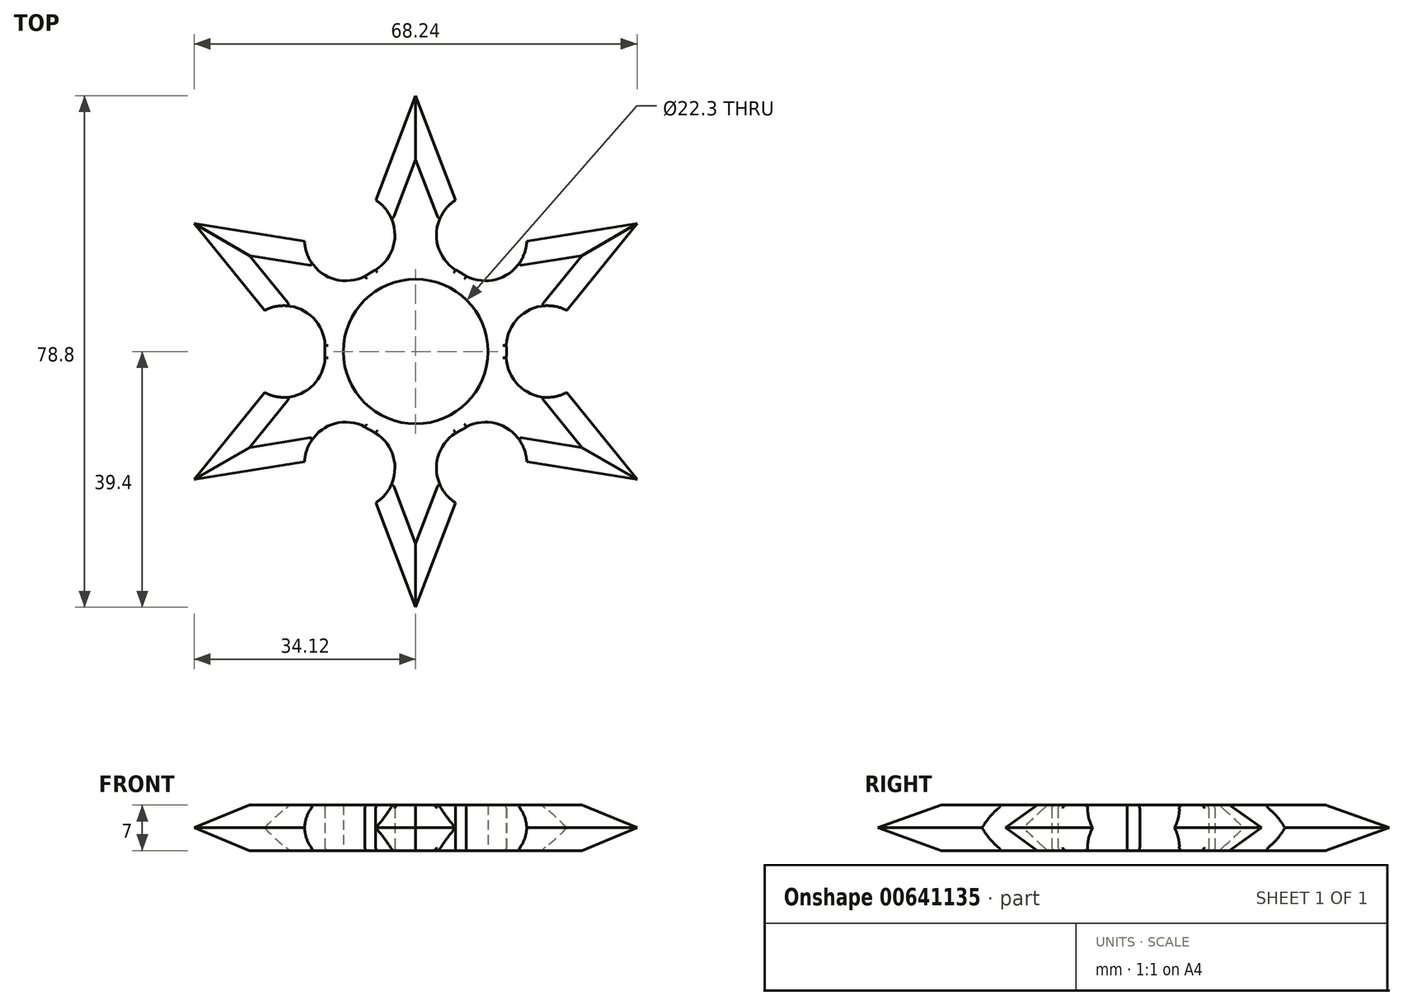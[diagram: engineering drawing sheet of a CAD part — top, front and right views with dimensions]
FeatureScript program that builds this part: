
annotation { "Feature Type Name" : "Feature", "Feature Type Description" : "" }
export const myFeature = defineFeature(function(context is Context, id is Id, definition is map)
    precondition{}
    {
        {
            var Q0;
            Q0=qCreatedBy(makeId("Top.planeOp"),FACE);
            var sketch = newSketch(context, id + "F0", { "sketchPlane" : qUnion([Q0])});
            skCircle(sketch, "E0", {"center": v(0, 0) * mm, "radius": 11.15 * mm});
            skCircle(sketch, "E1", {"center": v(0, 0) * mm, "radius": 14 * mm});
            skLineSegment(sketch, "E2", {"start": v(0, 0) * mm, "end": v(0, 43.6) * mm, "construction": true});
            skLineSegment(sketch, "E3.MirrorCS", {"start": v(0, 0) * mm, "end": v(37.76, -21.8) * mm, "construction": true});
            skLineSegment(sketch, "E4.MirrorCS", {"start": v(0, 0) * mm, "end": v(-37.76, -21.8) * mm, "construction": true});
            skLineSegment(sketch, "E5.MirrorCS", {"start": v(0, 0) * mm, "end": v(-37.76, 21.8) * mm, "construction": true});
            skLineSegment(sketch, "E6", {"start": v(0, 0) * mm, "end": v(0, -43.6) * mm, "construction": true});
            skLineSegment(sketch, "E7", {"start": v(20.76, 11.98) * mm, "end": v(24.5, 5.49) * mm});
            skLineSegment(sketch, "E8.MirrorCS", {"start": v(20.76, 11.98) * mm, "end": v(17, 18.48) * mm});
            skLineSegment(sketch, "E9", {"start": v(37.76, 21.8) * mm, "end": v(17, 18.48) * mm});
            skLineSegment(sketch, "E10", {"start": v(24.5, 5.49) * mm, "end": v(37.76, 21.8) * mm});
            skLineSegment(sketch, "E11", {"start": v(0, 0) * mm, "end": v(7, 12.12) * mm, "construction": true});
            skArc(sketch, "E12", {"start": v(7, 12.12) * mm, "mid": v(14.18, 11.88) * mm, "end": v(17, 18.48) * mm});
            skArc(sketch, "E13.MirrorCS", {"start": v(14, 0) * mm, "mid": v(17.38, 6.34) * mm, "end": v(24.5, 5.49) * mm});
            skLineSegment(sketch, "E14.MirrorCS", {"start": v(-37.76, 21.8) * mm, "end": v(-17, 18.48) * mm});
            skLineSegment(sketch, "E15.MirrorCS", {"start": v(-20.76, 11.98) * mm, "end": v(-17, 18.48) * mm});
            skArc(sketch, "E16.MirrorCS", {"start": v(-7, 12.12) * mm, "mid": v(-14.18, 11.88) * mm, "end": v(-17, 18.48) * mm});
            skArc(sketch, "E17.MirrorCS", {"start": v(-14, 0) * mm, "mid": v(-17.38, 6.34) * mm, "end": v(-24.5, 5.49) * mm});
            skLineSegment(sketch, "E18.MirrorCS", {"start": v(-20.76, 11.98) * mm, "end": v(-24.5, 5.49) * mm});
            skLineSegment(sketch, "E19.MirrorCS", {"start": v(-24.5, 5.49) * mm, "end": v(-37.76, 21.8) * mm});
            skArc(sketch, "E20.MirrorCS", {"start": v(7, -12.12) * mm, "mid": v(14.18, -11.88) * mm, "end": v(17, -18.48) * mm});
            skLineSegment(sketch, "E21.MirrorCS", {"start": v(37.76, -21.8) * mm, "end": v(17, -18.48) * mm});
            skLineSegment(sketch, "E22.MirrorCS", {"start": v(20.76, -11.98) * mm, "end": v(17, -18.48) * mm});
            skArc(sketch, "E23.MirrorCS", {"start": v(14, 0) * mm, "mid": v(17.38, -6.34) * mm, "end": v(24.5, -5.49) * mm});
            skLineSegment(sketch, "E24.MirrorCS", {"start": v(20.76, -11.98) * mm, "end": v(24.5, -5.49) * mm});
            skLineSegment(sketch, "E25.MirrorCS", {"start": v(24.5, -5.49) * mm, "end": v(37.76, -21.8) * mm});
            skArc(sketch, "E26.MirrorCS", {"start": v(-14, 0) * mm, "mid": v(-17.38, -6.34) * mm, "end": v(-24.5, -5.49) * mm});
            skLineSegment(sketch, "E27.MirrorCS", {"start": v(-20.76, -11.98) * mm, "end": v(-24.5, -5.49) * mm});
            skLineSegment(sketch, "E28.MirrorCS", {"start": v(-24.5, -5.49) * mm, "end": v(-37.76, -21.8) * mm});
            skLineSegment(sketch, "E29.MirrorCS", {"start": v(-37.76, -21.8) * mm, "end": v(-17, -18.48) * mm});
            skArc(sketch, "E30.MirrorCS", {"start": v(-7, -12.12) * mm, "mid": v(-14.18, -11.88) * mm, "end": v(-17, -18.48) * mm});
            skLineSegment(sketch, "E31.MirrorCS", {"start": v(-20.76, -11.98) * mm, "end": v(-17, -18.48) * mm});
            skLineSegment(sketch, "E32", {"start": v(0, 43.6) * mm, "end": v(0, 23.97) * mm});
            skLineSegment(sketch, "E33", {"start": v(0, 23.97) * mm, "end": v(7.5, 23.97) * mm});
            skLineSegment(sketch, "E34", {"start": v(0, 43.6) * mm, "end": v(7.5, 23.97) * mm});
            skLineSegment(sketch, "E35.MirrorCS", {"start": v(0, 43.6) * mm, "end": v(-7.5, 23.97) * mm});
            skLineSegment(sketch, "E36.MirrorCS", {"start": v(0, 23.97) * mm, "end": v(-7.5, 23.97) * mm});
            skLineSegment(sketch, "E37", {"start": v(0, 0) * mm, "end": v(-7, 12.12) * mm, "construction": true});
            skLineSegment(sketch, "E38.MirrorCS", {"start": v(0, -43.6) * mm, "end": v(-7.5, -23.97) * mm});
            skLineSegment(sketch, "E39.MirrorCS", {"start": v(0, -23.97) * mm, "end": v(-7.5, -23.97) * mm});
            skLineSegment(sketch, "E40.MirrorCS", {"start": v(0, -23.97) * mm, "end": v(7.5, -23.97) * mm});
            skLineSegment(sketch, "E41.MirrorCS", {"start": v(0, -43.6) * mm, "end": v(7.5, -23.97) * mm});
            skArc(sketch, "E42", {"start": v(7, -12.12) * mm, "mid": v(3.2, -18.22) * mm, "end": v(7.5, -23.97) * mm});
            skArc(sketch, "E43.MirrorCS", {"start": v(-7, -12.12) * mm, "mid": v(-3.2, -18.22) * mm, "end": v(-7.5, -23.97) * mm});
            skArc(sketch, "E44.MirrorCS", {"start": v(7, 12.12) * mm, "mid": v(3.2, 18.22) * mm, "end": v(7.5, 23.97) * mm});
            skArc(sketch, "E45.MirrorCS", {"start": v(-7, 12.12) * mm, "mid": v(-3.2, 18.22) * mm, "end": v(-7.5, 23.97) * mm});
            skLineSegment(sketch, "E46", {"start": v(37.76, 21.8) * mm, "end": v(0, 0) * mm, "construction": true});
            skSolve(sketch);
        }
        {
            var Q0;
            Q0=makeQuery(id+"F0.imprint","IMPRINT",FACE,{"disambiguationData":[TD([[makeQuery(id+"F0.imprint","IMPRINT",EDGE,{"derivedFrom":sQuery(id+"F0.wireOp",EDGE,"E32")}),1.0]])]});
            var Q1;
            Q1=makeQuery(id+"F0.imprint","IMPRINT",FACE,{"disambiguationData":[TD([[makeQuery(id+"F0.imprint","IMPRINT",EDGE,{"derivedFrom":sQuery(id+"F0.wireOp",EDGE,"E32")}),-1.0]])]});
            var Q2;
            {var subQ5=sQuery(id+"F0.wireOp",EDGE,"E36.MirrorCS");Q2=makeQuery(id+"F0.imprint","IMPRINT",FACE,{"disambiguationData":[TD([[makeQuery(id+"F0.imprint","IMPRINT",EDGE,{"derivedFrom":subQ5}),1.0]])]});}
            var Q3;
            {var subQ5=sQuery(id+"F0.wireOp",EDGE,"E33");Q3=makeQuery(id+"F0.imprint","IMPRINT",FACE,{"disambiguationData":[TD([[makeQuery(id+"F0.imprint","IMPRINT",EDGE,{"derivedFrom":subQ5}),-1.0]])]});}
            var Q4;
            {var subQ1=sQuery(id+"F0.wireOp",EDGE,"E0");var subQ7=sQuery(id+"F0.wireOp",EDGE,"E11");var subQ9=makeQuery(id+"F0.imprint","INTERSECT",VERTEX,{"derivedFrom":[subQ1,subQ7]});Q4=makeQuery(id+"F0.imprint","IMPRINT",FACE,{"disambiguationData":[TD([[makeQuery(id+"F0.imprint","IMPRINT",EDGE,{"disambiguationData":[TD([[subQ9,-1.0]])],"derivedFrom":subQ1}),-1.0]])]});}
            var Q5;
            {var subQ4=sQuery(id+"F0.wireOp",EDGE,"E0");var subQ7=sQuery(id+"F0.wireOp",EDGE,"E2");var subQ8=makeQuery(id+"F0.imprint","INTERSECT",VERTEX,{"derivedFrom":[subQ4,subQ7]});Q5=makeQuery(id+"F0.imprint","IMPRINT",FACE,{"disambiguationData":[TD([[makeQuery(id+"F0.imprint","IMPRINT",EDGE,{"disambiguationData":[TD([[subQ8,-1.0]])],"derivedFrom":subQ4}),-1.0]])]});}
            var Q6;
            {var subQ1=sQuery(id+"F0.wireOp",EDGE,"E0");var subQ5=sQuery(id+"F0.wireOp",EDGE,"E37");var subQ6=makeQuery(id+"F0.imprint","INTERSECT",VERTEX,{"derivedFrom":[subQ1,subQ5]});Q6=makeQuery(id+"F0.imprint","IMPRINT",FACE,{"disambiguationData":[TD([[makeQuery(id+"F0.imprint","IMPRINT",EDGE,{"disambiguationData":[TD([[subQ6,-1.0]])],"derivedFrom":subQ1}),-1.0]])]});}
            var Q7;
            {var subQ5=sQuery(id+"F0.wireOp",EDGE,"E15.MirrorCS");Q7=makeQuery(id+"F0.imprint","IMPRINT",FACE,{"disambiguationData":[TD([[makeQuery(id+"F0.imprint","IMPRINT",EDGE,{"derivedFrom":subQ5}),-1.0]])]});}
            var Q8;
            {var subQ5=sQuery(id+"F0.wireOp",EDGE,"E0");var subQ9=sQuery(id+"F0.wireOp",EDGE,"E5.MirrorCS");var subQ11=makeQuery(id+"F0.imprint","INTERSECT",VERTEX,{"derivedFrom":[subQ5,subQ9]});Q8=makeQuery(id+"F0.imprint","IMPRINT",FACE,{"disambiguationData":[TD([[makeQuery(id+"F0.imprint","IMPRINT",EDGE,{"disambiguationData":[TD([[subQ11,-1.0]])],"derivedFrom":subQ5}),-1.0]])]});}
            var Q9;
            {var subQ2=sQuery(id+"F0.wireOp",EDGE,"E27.MirrorCS");Q9=makeQuery(id+"F0.imprint","IMPRINT",FACE,{"disambiguationData":[TD([[makeQuery(id+"F0.imprint","IMPRINT",EDGE,{"derivedFrom":subQ2}),1.0]])]});}
            var Q10;
            {var subQ1=sQuery(id+"F0.wireOp",EDGE,"E11");var subQ4=sQuery(id+"F0.wireOp",EDGE,"E0");var subQ5=makeQuery(id+"F0.imprint","INTERSECT",VERTEX,{"derivedFrom":[subQ4,subQ1]});Q10=makeQuery(id+"F0.imprint","IMPRINT",FACE,{"disambiguationData":[TD([[makeQuery(id+"F0.imprint","IMPRINT",EDGE,{"disambiguationData":[TD([[subQ5,1.0]])],"derivedFrom":subQ4}),-1.0]])]});}
            var Q11;
            {var subQ5=sQuery(id+"F0.wireOp",EDGE,"E40.MirrorCS");Q11=makeQuery(id+"F0.imprint","IMPRINT",FACE,{"disambiguationData":[TD([[makeQuery(id+"F0.imprint","IMPRINT",EDGE,{"derivedFrom":subQ5}),1.0]])]});}
            var Q12;
            {var subQ5=sQuery(id+"F0.wireOp",EDGE,"E6");var subQ6=sQuery(id+"F0.wireOp",EDGE,"E0");var subQ7=makeQuery(id+"F0.imprint","INTERSECT",VERTEX,{"derivedFrom":[subQ6,subQ5]});Q12=makeQuery(id+"F0.imprint","IMPRINT",FACE,{"disambiguationData":[TD([[makeQuery(id+"F0.imprint","IMPRINT",EDGE,{"disambiguationData":[TD([[subQ7,-1.0]])],"derivedFrom":subQ6}),-1.0]])]});}
            var Q13;
            {var subQ5=sQuery(id+"F0.wireOp",EDGE,"E18.MirrorCS");Q13=makeQuery(id+"F0.imprint","IMPRINT",FACE,{"disambiguationData":[TD([[makeQuery(id+"F0.imprint","IMPRINT",EDGE,{"derivedFrom":subQ5}),1.0]])]});}
            var Q14;
            {var subQ5=sQuery(id+"F0.wireOp",EDGE,"E31.MirrorCS");Q14=makeQuery(id+"F0.imprint","IMPRINT",FACE,{"disambiguationData":[TD([[makeQuery(id+"F0.imprint","IMPRINT",EDGE,{"derivedFrom":subQ5}),1.0]])]});}
            var Q15;
            {var subQ5=sQuery(id+"F0.wireOp",EDGE,"E22.MirrorCS");Q15=makeQuery(id+"F0.imprint","IMPRINT",FACE,{"disambiguationData":[TD([[makeQuery(id+"F0.imprint","IMPRINT",EDGE,{"derivedFrom":subQ5}),-1.0]])]});}
            var Q16;
            {var subQ2=sQuery(id+"F0.wireOp",EDGE,"E24.MirrorCS");Q16=makeQuery(id+"F0.imprint","IMPRINT",FACE,{"disambiguationData":[TD([[makeQuery(id+"F0.imprint","IMPRINT",EDGE,{"derivedFrom":subQ2}),-1.0]])]});}
            var Q17;
            {var subQ0=sQuery(id+"F0.wireOp",EDGE,"E21.MirrorCS");Q17=makeQuery(id+"F0.imprint","IMPRINT",FACE,{"disambiguationData":[TD([[makeQuery(id+"F0.imprint","IMPRINT",EDGE,{"derivedFrom":subQ0}),-1.0]])]});}
            var Q18;
            {var subQ5=sQuery(id+"F0.wireOp",EDGE,"E39.MirrorCS");Q18=makeQuery(id+"F0.imprint","IMPRINT",FACE,{"disambiguationData":[TD([[makeQuery(id+"F0.imprint","IMPRINT",EDGE,{"derivedFrom":subQ5}),-1.0]])]});}
            var Q19;
            {var subQ5=sQuery(id+"F0.wireOp",EDGE,"E7");Q19=makeQuery(id+"F0.imprint","IMPRINT",FACE,{"disambiguationData":[TD([[makeQuery(id+"F0.imprint","IMPRINT",EDGE,{"derivedFrom":subQ5}),-1.0]])]});}
            var Q20;
            {var subQ2=sQuery(id+"F0.wireOp",EDGE,"E18.MirrorCS");Q20=makeQuery(id+"F0.imprint","IMPRINT",FACE,{"disambiguationData":[TD([[makeQuery(id+"F0.imprint","IMPRINT",EDGE,{"derivedFrom":subQ2}),-1.0]])]});}
            var Q21;
            {var subQ0=sQuery(id+"F0.wireOp",EDGE,"E4.MirrorCS");var subQ1=sQuery(id+"F0.wireOp",EDGE,"E0");var subQ2=makeQuery(id+"F0.imprint","INTERSECT",VERTEX,{"derivedFrom":[subQ1,subQ0]});Q21=makeQuery(id+"F0.imprint","IMPRINT",FACE,{"disambiguationData":[TD([[makeQuery(id+"F0.imprint","IMPRINT",EDGE,{"disambiguationData":[TD([[subQ2,-1.0]])],"derivedFrom":subQ1}),-1.0]])]});}
            var Q22;
            {var subQ5=sQuery(id+"F0.wireOp",EDGE,"E8.MirrorCS");Q22=makeQuery(id+"F0.imprint","IMPRINT",FACE,{"disambiguationData":[TD([[makeQuery(id+"F0.imprint","IMPRINT",EDGE,{"derivedFrom":subQ5}),1.0]])]});}
            var Q23;
            {var subQ5=sQuery(id+"F0.wireOp",EDGE,"E24.MirrorCS");Q23=makeQuery(id+"F0.imprint","IMPRINT",FACE,{"disambiguationData":[TD([[makeQuery(id+"F0.imprint","IMPRINT",EDGE,{"derivedFrom":subQ5}),1.0]])]});}
            var Q24;
            {var subQ3=sQuery(id+"F0.wireOp",EDGE,"E8.MirrorCS");Q24=makeQuery(id+"F0.imprint","IMPRINT",FACE,{"disambiguationData":[TD([[makeQuery(id+"F0.imprint","IMPRINT",EDGE,{"derivedFrom":subQ3}),-1.0]])]});}
            var Q25;
            {var subQ0=sQuery(id+"F0.wireOp",EDGE,"E14.MirrorCS");Q25=makeQuery(id+"F0.imprint","IMPRINT",FACE,{"disambiguationData":[TD([[makeQuery(id+"F0.imprint","IMPRINT",EDGE,{"derivedFrom":subQ0}),-1.0]])]});}
            var Q26;
            {var subQ0=sQuery(id+"F0.wireOp",EDGE,"E29.MirrorCS");Q26=makeQuery(id+"F0.imprint","IMPRINT",FACE,{"disambiguationData":[TD([[makeQuery(id+"F0.imprint","IMPRINT",EDGE,{"derivedFrom":subQ0}),1.0]])]});}
            var Q27;
            {var subQ5=sQuery(id+"F0.wireOp",EDGE,"E27.MirrorCS");Q27=makeQuery(id+"F0.imprint","IMPRINT",FACE,{"disambiguationData":[TD([[makeQuery(id+"F0.imprint","IMPRINT",EDGE,{"derivedFrom":subQ5}),-1.0]])]});}
            var Q28;
            {var subQ3=sQuery(id+"F0.wireOp",EDGE,"E7");Q28=makeQuery(id+"F0.imprint","IMPRINT",FACE,{"disambiguationData":[TD([[makeQuery(id+"F0.imprint","IMPRINT",EDGE,{"derivedFrom":subQ3}),1.0]])]});}
            var Q29;
            {var subQ0=sQuery(id+"F0.wireOp",EDGE,"E38.MirrorCS");Q29=makeQuery(id+"F0.imprint","IMPRINT",FACE,{"disambiguationData":[TD([[makeQuery(id+"F0.imprint","IMPRINT",EDGE,{"derivedFrom":subQ0}),-1.0]])]});}
            var Q30;
            {var subQ1=sQuery(id+"F0.wireOp",EDGE,"E0");var subQ9=sQuery(id+"F0.wireOp",EDGE,"bd304282-317b-458c-878f-7ac9d7db5be70.MirrorCS");var subQ12=makeQuery(id+"F0.imprint","INTERSECT",VERTEX,{"derivedFrom":[subQ1,subQ9]});Q30=makeQuery(id+"F0.imprint","IMPRINT",FACE,{"disambiguationData":[TD([[makeQuery(id+"F0.imprint","IMPRINT",EDGE,{"disambiguationData":[TD([[subQ12,1.0]])],"derivedFrom":subQ1}),-1.0]])]});}
            var Q31;
            {var subQ2=sQuery(id+"F0.wireOp",EDGE,"E40.MirrorCS");Q31=makeQuery(id+"F0.imprint","IMPRINT",FACE,{"disambiguationData":[TD([[makeQuery(id+"F0.imprint","IMPRINT",EDGE,{"derivedFrom":subQ2}),-1.0]])]});}
            var Q32;
            {var subQ0=sQuery(id+"F0.wireOp",EDGE,"E42");var subQ1=sQuery(id+"F0.wireOp",EDGE,"E1");var subQ3=makeQuery(id+"F0.imprint","INTERSECT",VERTEX,{"derivedFrom":[subQ1,subQ0]});Q32=makeQuery(id+"F0.imprint","IMPRINT",FACE,{"disambiguationData":[TD([[makeQuery(id+"F0.imprint","IMPRINT",EDGE,{"disambiguationData":[TD([[subQ3,-1.0]])],"derivedFrom":subQ1}),1.0]])]});}
            var Q33;
            {var subQ0=sQuery(id+"F0.wireOp",EDGE,"E23.MirrorCS");var subQ1=sQuery(id+"F0.wireOp",EDGE,"E1");var subQ3=makeQuery(id+"F0.imprint","INTERSECT",VERTEX,{"derivedFrom":[subQ1,subQ0]});Q33=makeQuery(id+"F0.imprint","IMPRINT",FACE,{"disambiguationData":[TD([[makeQuery(id+"F0.imprint","IMPRINT",EDGE,{"disambiguationData":[TD([[subQ3,-1.0]])],"derivedFrom":subQ1}),1.0]])]});}
            var Q34;
            {var subQ0=sQuery(id+"F0.wireOp",EDGE,"E20.MirrorCS");var subQ1=sQuery(id+"F0.wireOp",EDGE,"E1");var subQ3=makeQuery(id+"F0.imprint","INTERSECT",VERTEX,{"derivedFrom":[subQ1,subQ0]});Q34=makeQuery(id+"F0.imprint","IMPRINT",FACE,{"disambiguationData":[TD([[makeQuery(id+"F0.imprint","IMPRINT",EDGE,{"disambiguationData":[TD([[subQ3,1.0]])],"derivedFrom":subQ1}),1.0]])]});}
            var Q35;
            {var subQ0=sQuery(id+"F0.wireOp",EDGE,"E30.MirrorCS");var subQ1=sQuery(id+"F0.wireOp",EDGE,"E1");var subQ3=makeQuery(id+"F0.imprint","INTERSECT",VERTEX,{"derivedFrom":[subQ1,subQ0]});Q35=makeQuery(id+"F0.imprint","IMPRINT",FACE,{"disambiguationData":[TD([[makeQuery(id+"F0.imprint","IMPRINT",EDGE,{"disambiguationData":[TD([[subQ3,-1.0]])],"derivedFrom":subQ1}),1.0]])]});}
            var Q36;
            {var subQ0=sQuery(id+"F0.wireOp",EDGE,"E43.MirrorCS");var subQ1=sQuery(id+"F0.wireOp",EDGE,"E1");var subQ3=makeQuery(id+"F0.imprint","INTERSECT",VERTEX,{"derivedFrom":[subQ1,subQ0]});Q36=makeQuery(id+"F0.imprint","IMPRINT",FACE,{"disambiguationData":[TD([[makeQuery(id+"F0.imprint","IMPRINT",EDGE,{"disambiguationData":[TD([[subQ3,1.0]])],"derivedFrom":subQ1}),1.0]])]});}
            var Q37;
            {var subQ0=sQuery(id+"F0.wireOp",EDGE,"E26.MirrorCS");var subQ1=sQuery(id+"F0.wireOp",EDGE,"E1");var subQ3=makeQuery(id+"F0.imprint","INTERSECT",VERTEX,{"derivedFrom":[subQ1,subQ0]});Q37=makeQuery(id+"F0.imprint","IMPRINT",FACE,{"disambiguationData":[TD([[makeQuery(id+"F0.imprint","IMPRINT",EDGE,{"disambiguationData":[TD([[subQ3,1.0]])],"derivedFrom":subQ1}),1.0]])]});}
            var Q38;
            {var subQ0=sQuery(id+"F0.wireOp",EDGE,"E17.MirrorCS");var subQ1=sQuery(id+"F0.wireOp",EDGE,"E1");var subQ3=makeQuery(id+"F0.imprint","INTERSECT",VERTEX,{"derivedFrom":[subQ1,subQ0]});Q38=makeQuery(id+"F0.imprint","IMPRINT",FACE,{"disambiguationData":[TD([[makeQuery(id+"F0.imprint","IMPRINT",EDGE,{"disambiguationData":[TD([[subQ3,-1.0]])],"derivedFrom":subQ1}),1.0]])]});}
            var Q39;
            {var subQ0=sQuery(id+"F0.wireOp",EDGE,"E13.MirrorCS");var subQ1=sQuery(id+"F0.wireOp",EDGE,"E1");var subQ3=makeQuery(id+"F0.imprint","INTERSECT",VERTEX,{"derivedFrom":[subQ1,subQ0]});Q39=makeQuery(id+"F0.imprint","IMPRINT",FACE,{"disambiguationData":[TD([[makeQuery(id+"F0.imprint","IMPRINT",EDGE,{"disambiguationData":[TD([[subQ3,1.0]])],"derivedFrom":subQ1}),1.0]])]});}
            var Q40;
            {var subQ0=sQuery(id+"F0.wireOp",EDGE,"E45.MirrorCS");var subQ1=sQuery(id+"F0.wireOp",EDGE,"E1");var subQ3=makeQuery(id+"F0.imprint","INTERSECT",VERTEX,{"derivedFrom":[subQ1,subQ0]});Q40=makeQuery(id+"F0.imprint","IMPRINT",FACE,{"disambiguationData":[TD([[makeQuery(id+"F0.imprint","IMPRINT",EDGE,{"disambiguationData":[TD([[subQ3,-1.0]])],"derivedFrom":subQ1}),1.0]])]});}
            var Q41;
            {var subQ0=sQuery(id+"F0.wireOp",EDGE,"E16.MirrorCS");var subQ1=sQuery(id+"F0.wireOp",EDGE,"E1");var subQ3=makeQuery(id+"F0.imprint","INTERSECT",VERTEX,{"derivedFrom":[subQ1,subQ0]});Q41=makeQuery(id+"F0.imprint","IMPRINT",FACE,{"disambiguationData":[TD([[makeQuery(id+"F0.imprint","IMPRINT",EDGE,{"disambiguationData":[TD([[subQ3,1.0]])],"derivedFrom":subQ1}),1.0]])]});}
            var Q42;
            {var subQ0=sQuery(id+"F0.wireOp",EDGE,"E44.MirrorCS");var subQ1=sQuery(id+"F0.wireOp",EDGE,"E1");var subQ3=makeQuery(id+"F0.imprint","INTERSECT",VERTEX,{"derivedFrom":[subQ1,subQ0]});Q42=makeQuery(id+"F0.imprint","IMPRINT",FACE,{"disambiguationData":[TD([[makeQuery(id+"F0.imprint","IMPRINT",EDGE,{"disambiguationData":[TD([[subQ3,1.0]])],"derivedFrom":subQ1}),1.0]])]});}
            var Q43;
            {var subQ0=sQuery(id+"F0.wireOp",EDGE,"E12");var subQ1=sQuery(id+"F0.wireOp",EDGE,"E1");var subQ3=makeQuery(id+"F0.imprint","INTERSECT",VERTEX,{"derivedFrom":[subQ1,subQ0]});Q43=makeQuery(id+"F0.imprint","IMPRINT",FACE,{"disambiguationData":[TD([[makeQuery(id+"F0.imprint","IMPRINT",EDGE,{"disambiguationData":[TD([[subQ3,-1.0]])],"derivedFrom":subQ1}),1.0]])]});}
            var Q44;
            Q44=makeQuery(id+"F0.imprint","IMPRINT",FACE,{"disambiguationData":[TD([[makeQuery(id+"F0.imprint","IMPRINT",EDGE,{"derivedFrom":sQuery(id+"F0.wireOp",EDGE,"p3hnCSgG-ZrtL-qWsR-BndH-5srnAVTTJyzc")}),1.0]])]});
            extrude(context, id + "F1", {"entities" : qUnion([Q0, Q1, Q2, Q3, Q4, Q5, Q6, Q7, Q8, Q9, Q10, Q11, Q12, Q13, Q14, Q15, Q16, Q17, Q18, Q19, Q20, Q21, Q22, Q23, Q24, Q25, Q26, Q27, Q28, Q29, Q30, Q31, Q32, Q33, Q34, Q35, Q36, Q37, Q38, Q39, Q40, Q41, Q42, Q43, Q44]), "depth" : 7 * mm, "offsetDistance" : 25 * mm});
        }
        {
            var Q0;
            Q0=makeQuery(id+"F1.opExtrude","CAP_EDGE",EDGE,{"disambiguationData":[OSD([sQuery(id+"F0.wireOp",EDGE,"E21.MirrorCS")])],"isStart":false});
            var Q1;
            Q1=makeQuery(id+"F1.opExtrude","CAP_EDGE",EDGE,{"disambiguationData":[OSD([sQuery(id+"F0.wireOp",EDGE,"E25.MirrorCS")])],"isStart":false});
            var Q2;
            Q2=makeQuery(id+"F1.opExtrude","CAP_EDGE",EDGE,{"disambiguationData":[OSD([sQuery(id+"F0.wireOp",EDGE,"E41.MirrorCS")])],"isStart":false});
            var Q3;
            Q3=makeQuery(id+"F1.opExtrude","CAP_EDGE",EDGE,{"disambiguationData":[OSD([sQuery(id+"F0.wireOp",EDGE,"E29.MirrorCS")])],"isStart":false});
            var Q4;
            Q4=makeQuery(id+"F1.opExtrude","CAP_EDGE",EDGE,{"disambiguationData":[OSD([sQuery(id+"F0.wireOp",EDGE,"E19.MirrorCS")])],"isStart":false});
            var Q5;
            Q5=makeQuery(id+"F1.opExtrude","CAP_EDGE",EDGE,{"disambiguationData":[OSD([sQuery(id+"F0.wireOp",EDGE,"E35.MirrorCS")])],"isStart":false});
            var Q6;
            Q6=makeQuery(id+"F1.opExtrude","CAP_EDGE",EDGE,{"disambiguationData":[OSD([sQuery(id+"F0.wireOp",EDGE,"E9")])],"isStart":false});
            chamfer(context, id + "F2", {"entities" : qUnion([Q0, Q1, Q2, Q3, Q4, Q5, Q6]), "width" : 5 * mm, "tangentPropagation" : true});
        }
        {
            var Q0;
            Q0=makeQuery(id+"F1.opExtrude","CAP_EDGE",EDGE,{"disambiguationData":[OSD([sQuery(id+"F0.wireOp",EDGE,"E34")])],"isStart":false});
            var Q1;
            Q1=makeQuery(id+"F1.opExtrude","CAP_EDGE",EDGE,{"disambiguationData":[OSD([sQuery(id+"F0.wireOp",EDGE,"E14.MirrorCS")])],"isStart":false});
            var Q2;
            Q2=makeQuery(id+"F1.opExtrude","CAP_EDGE",EDGE,{"disambiguationData":[OSD([sQuery(id+"F0.wireOp",EDGE,"E28.MirrorCS")])],"isStart":false});
            var Q3;
            Q3=makeQuery(id+"F1.opExtrude","CAP_EDGE",EDGE,{"disambiguationData":[OSD([sQuery(id+"F0.wireOp",EDGE,"E38.MirrorCS")])],"isStart":false});
            var Q4;
            Q4=makeQuery(id+"F1.opExtrude","CAP_EDGE",EDGE,{"disambiguationData":[OSD([sQuery(id+"F0.wireOp",EDGE,"E10")])],"isStart":false});
            chamfer(context, id + "F3", {"entities" : qUnion([Q0, Q1, Q2, Q3, Q4]), "width" : 5 * mm, "tangentPropagation" : true});
        }
        {
            var Q0;
            Q0=makeQuery(id+"F1.opExtrude","CAP_EDGE",EDGE,{"disambiguationData":[OSD([sQuery(id+"F0.wireOp",EDGE,"E38.MirrorCS")])],"isStart":true});
            var Q1;
            Q1=makeQuery(id+"F1.opExtrude","CAP_EDGE",EDGE,{"disambiguationData":[OSD([sQuery(id+"F0.wireOp",EDGE,"E21.MirrorCS")])],"isStart":true});
            var Q2;
            Q2=makeQuery(id+"F1.opExtrude","CAP_EDGE",EDGE,{"disambiguationData":[OSD([sQuery(id+"F0.wireOp",EDGE,"E10")])],"isStart":true});
            var Q3;
            Q3=makeQuery(id+"F1.opExtrude","CAP_EDGE",EDGE,{"disambiguationData":[OSD([sQuery(id+"F0.wireOp",EDGE,"E34")])],"isStart":true});
            var Q4;
            Q4=makeQuery(id+"F1.opExtrude","CAP_EDGE",EDGE,{"disambiguationData":[OSD([sQuery(id+"F0.wireOp",EDGE,"E14.MirrorCS")])],"isStart":true});
            var Q5;
            Q5=makeQuery(id+"F1.opExtrude","CAP_EDGE",EDGE,{"disambiguationData":[OSD([sQuery(id+"F0.wireOp",EDGE,"E28.MirrorCS")])],"isStart":true});
            chamfer(context, id + "F4", {"entities" : qUnion([Q0, Q1, Q2, Q3, Q4, Q5]), "width" : 5 * mm, "tangentPropagation" : true});
        }
        {
            var Q0;
            Q0=makeQuery(id+"F1.opExtrude","CAP_EDGE",EDGE,{"disambiguationData":[OSD([sQuery(id+"F0.wireOp",EDGE,"E19.MirrorCS")])],"isStart":true});
            var Q1;
            Q1=makeQuery(id+"F1.opExtrude","CAP_EDGE",EDGE,{"disambiguationData":[OSD([sQuery(id+"F0.wireOp",EDGE,"E29.MirrorCS")])],"isStart":true});
            var Q2;
            Q2=makeQuery(id+"F1.opExtrude","CAP_EDGE",EDGE,{"disambiguationData":[OSD([sQuery(id+"F0.wireOp",EDGE,"E41.MirrorCS")])],"isStart":true});
            var Q3;
            Q3=makeQuery(id+"F1.opExtrude","CAP_EDGE",EDGE,{"disambiguationData":[OSD([sQuery(id+"F0.wireOp",EDGE,"E25.MirrorCS")])],"isStart":true});
            var Q4;
            Q4=makeQuery(id+"F1.opExtrude","CAP_EDGE",EDGE,{"disambiguationData":[OSD([sQuery(id+"F0.wireOp",EDGE,"E9")])],"isStart":true});
            var Q5;
            Q5=makeQuery(id+"F1.opExtrude","CAP_EDGE",EDGE,{"disambiguationData":[OSD([sQuery(id+"F0.wireOp",EDGE,"E35.MirrorCS")])],"isStart":true});
            chamfer(context, id + "F5", {"entities" : qUnion([Q0, Q1, Q2, Q3, Q4, Q5]), "width" : 5 * mm, "tangentPropagation" : true});
        }
        {
            var Q0;
            Q0=makeQuery(id+"F1.opExtrude","CAP_EDGE",EDGE,{"disambiguationData":[OSD([sQuery(id+"F0.wireOp",EDGE,"E26.MirrorCS")])],"isStart":false});
            var Q1;
            {var subQ0=sQuery(id+"F0.wireOp",EDGE,"E26.MirrorCS");var subQ1=sQuery(id+"F0.wireOp",EDGE,"E17.MirrorCS");var subQ2=sQuery(id+"F0.wireOp",EDGE,"E1");Q1=makeQuery(id+"F1.opExtrude","CAP_EDGE",EDGE,{"disambiguationData":[OSD([subQ2]),TDD([makeQuery(id+"F0.imprint","IMPRINT",EDGE,{"disambiguationData":[TD([[makeQuery(id+"F0.imprint","INTERSECT",VERTEX,{"derivedFrom":[subQ2,subQ1]}),-1.0]])],"derivedFrom":subQ2}),makeQuery(id+"F0.imprint","IMPRINT",EDGE,{"disambiguationData":[TD([[makeQuery(id+"F0.imprint","INTERSECT",VERTEX,{"derivedFrom":[subQ2,subQ0]}),1.0]])],"derivedFrom":subQ2})])],"isStart":false});}
            var Q2;
            Q2=makeQuery(id+"F1.opExtrude","CAP_EDGE",EDGE,{"disambiguationData":[OSD([sQuery(id+"F0.wireOp",EDGE,"E17.MirrorCS")])],"isStart":false});
            var Q3;
            Q3=makeQuery(id+"F1.opExtrude","CAP_EDGE",EDGE,{"disambiguationData":[OSD([sQuery(id+"F0.wireOp",EDGE,"E16.MirrorCS")])],"isStart":false});
            var Q4;
            {var subQ0=sQuery(id+"F0.wireOp",EDGE,"E45.MirrorCS");var subQ1=sQuery(id+"F0.wireOp",EDGE,"E16.MirrorCS");var subQ2=sQuery(id+"F0.wireOp",EDGE,"E1");Q4=makeQuery(id+"F1.opExtrude","CAP_EDGE",EDGE,{"disambiguationData":[OSD([subQ2]),TDD([makeQuery(id+"F0.imprint","IMPRINT",EDGE,{"disambiguationData":[TD([[makeQuery(id+"F0.imprint","INTERSECT",VERTEX,{"derivedFrom":[subQ2,subQ0]}),-1.0]])],"derivedFrom":subQ2}),makeQuery(id+"F0.imprint","IMPRINT",EDGE,{"disambiguationData":[TD([[makeQuery(id+"F0.imprint","INTERSECT",VERTEX,{"derivedFrom":[subQ2,subQ1]}),1.0]])],"derivedFrom":subQ2})])],"isStart":false});}
            var Q5;
            Q5=makeQuery(id+"F1.opExtrude","CAP_EDGE",EDGE,{"disambiguationData":[OSD([sQuery(id+"F0.wireOp",EDGE,"E45.MirrorCS")])],"isStart":false});
            var Q6;
            Q6=makeQuery(id+"F1.opExtrude","CAP_EDGE",EDGE,{"disambiguationData":[OSD([sQuery(id+"F0.wireOp",EDGE,"E44.MirrorCS")])],"isStart":false});
            var Q7;
            {var subQ0=sQuery(id+"F0.wireOp",EDGE,"E44.MirrorCS");var subQ1=sQuery(id+"F0.wireOp",EDGE,"E12");var subQ2=sQuery(id+"F0.wireOp",EDGE,"E1");Q7=makeQuery(id+"F1.opExtrude","CAP_EDGE",EDGE,{"disambiguationData":[OSD([subQ2]),TDD([makeQuery(id+"F0.imprint","IMPRINT",EDGE,{"disambiguationData":[TD([[makeQuery(id+"F0.imprint","INTERSECT",VERTEX,{"derivedFrom":[subQ2,subQ1]}),-1.0]])],"derivedFrom":subQ2}),makeQuery(id+"F0.imprint","IMPRINT",EDGE,{"disambiguationData":[TD([[makeQuery(id+"F0.imprint","INTERSECT",VERTEX,{"derivedFrom":[subQ2,subQ0]}),1.0]])],"derivedFrom":subQ2})])],"isStart":false});}
            var Q8;
            Q8=makeQuery(id+"F1.opExtrude","CAP_EDGE",EDGE,{"disambiguationData":[OSD([sQuery(id+"F0.wireOp",EDGE,"E12")])],"isStart":false});
            var Q9;
            Q9=makeQuery(id+"F1.opExtrude","CAP_EDGE",EDGE,{"disambiguationData":[OSD([sQuery(id+"F0.wireOp",EDGE,"E13.MirrorCS")])],"isStart":false});
            var Q10;
            {var subQ0=sQuery(id+"F0.wireOp",EDGE,"E23.MirrorCS");var subQ1=sQuery(id+"F0.wireOp",EDGE,"E13.MirrorCS");var subQ2=sQuery(id+"F0.wireOp",EDGE,"E1");Q10=makeQuery(id+"F1.opExtrude","CAP_EDGE",EDGE,{"disambiguationData":[OSD([subQ2]),TDD([makeQuery(id+"F0.imprint","IMPRINT",EDGE,{"disambiguationData":[TD([[makeQuery(id+"F0.imprint","INTERSECT",VERTEX,{"derivedFrom":[subQ2,subQ1]}),1.0]])],"derivedFrom":subQ2}),makeQuery(id+"F0.imprint","IMPRINT",EDGE,{"disambiguationData":[TD([[makeQuery(id+"F0.imprint","INTERSECT",VERTEX,{"derivedFrom":[subQ2,subQ0]}),-1.0]])],"derivedFrom":subQ2})])],"isStart":false});}
            var Q11;
            Q11=makeQuery(id+"F1.opExtrude","CAP_EDGE",EDGE,{"disambiguationData":[OSD([sQuery(id+"F0.wireOp",EDGE,"E23.MirrorCS")])],"isStart":false});
            var Q12;
            Q12=makeQuery(id+"F1.opExtrude","CAP_EDGE",EDGE,{"disambiguationData":[OSD([sQuery(id+"F0.wireOp",EDGE,"E20.MirrorCS")])],"isStart":false});
            var Q13;
            {var subQ0=sQuery(id+"F0.wireOp",EDGE,"E42");var subQ1=sQuery(id+"F0.wireOp",EDGE,"E20.MirrorCS");var subQ2=sQuery(id+"F0.wireOp",EDGE,"E1");Q13=makeQuery(id+"F1.opExtrude","CAP_EDGE",EDGE,{"disambiguationData":[OSD([subQ2]),TDD([makeQuery(id+"F0.imprint","IMPRINT",EDGE,{"disambiguationData":[TD([[makeQuery(id+"F0.imprint","INTERSECT",VERTEX,{"derivedFrom":[subQ2,subQ0]}),-1.0]])],"derivedFrom":subQ2}),makeQuery(id+"F0.imprint","IMPRINT",EDGE,{"disambiguationData":[TD([[makeQuery(id+"F0.imprint","INTERSECT",VERTEX,{"derivedFrom":[subQ2,subQ1]}),1.0]])],"derivedFrom":subQ2})])],"isStart":false});}
            var Q14;
            Q14=makeQuery(id+"F1.opExtrude","CAP_EDGE",EDGE,{"disambiguationData":[OSD([sQuery(id+"F0.wireOp",EDGE,"E42")])],"isStart":false});
            var Q15;
            Q15=makeQuery(id+"F1.opExtrude","CAP_EDGE",EDGE,{"disambiguationData":[OSD([sQuery(id+"F0.wireOp",EDGE,"E43.MirrorCS")])],"isStart":false});
            var Q16;
            {var subQ0=sQuery(id+"F0.wireOp",EDGE,"E43.MirrorCS");var subQ1=sQuery(id+"F0.wireOp",EDGE,"E30.MirrorCS");var subQ2=sQuery(id+"F0.wireOp",EDGE,"E1");Q16=makeQuery(id+"F1.opExtrude","CAP_EDGE",EDGE,{"disambiguationData":[OSD([subQ2]),TDD([makeQuery(id+"F0.imprint","IMPRINT",EDGE,{"disambiguationData":[TD([[makeQuery(id+"F0.imprint","INTERSECT",VERTEX,{"derivedFrom":[subQ2,subQ1]}),-1.0]])],"derivedFrom":subQ2}),makeQuery(id+"F0.imprint","IMPRINT",EDGE,{"disambiguationData":[TD([[makeQuery(id+"F0.imprint","INTERSECT",VERTEX,{"derivedFrom":[subQ2,subQ0]}),1.0]])],"derivedFrom":subQ2})])],"isStart":false});}
            var Q17;
            Q17=makeQuery(id+"F1.opExtrude","CAP_EDGE",EDGE,{"disambiguationData":[OSD([sQuery(id+"F0.wireOp",EDGE,"E30.MirrorCS")])],"isStart":false});
            fillet(context, id + "F6", {"entities" : qUnion([Q0, Q1, Q2, Q3, Q4, Q5, Q6, Q7, Q8, Q9, Q10, Q11, Q12, Q13, Q14, Q15, Q16, Q17]), "radius" : .5 * mm, "tangentPropagation" : true, "allowEdgeOverflow" : false});
        }
        {
            var Q0;
            Q0=makeQuery(id+"F1.opExtrude","CAP_EDGE",EDGE,{"disambiguationData":[OSD([sQuery(id+"F0.wireOp",EDGE,"E45.MirrorCS")])],"isStart":true});
            var Q1;
            {var subQ0=sQuery(id+"F0.wireOp",EDGE,"E45.MirrorCS");var subQ1=sQuery(id+"F0.wireOp",EDGE,"E16.MirrorCS");var subQ2=sQuery(id+"F0.wireOp",EDGE,"E1");Q1=makeQuery(id+"F1.opExtrude","CAP_EDGE",EDGE,{"disambiguationData":[OSD([subQ2]),TDD([makeQuery(id+"F0.imprint","IMPRINT",EDGE,{"disambiguationData":[TD([[makeQuery(id+"F0.imprint","INTERSECT",VERTEX,{"derivedFrom":[subQ2,subQ0]}),-1.0]])],"derivedFrom":subQ2}),makeQuery(id+"F0.imprint","IMPRINT",EDGE,{"disambiguationData":[TD([[makeQuery(id+"F0.imprint","INTERSECT",VERTEX,{"derivedFrom":[subQ2,subQ1]}),1.0]])],"derivedFrom":subQ2})])],"isStart":true});}
            var Q2;
            Q2=makeQuery(id+"F1.opExtrude","CAP_EDGE",EDGE,{"disambiguationData":[OSD([sQuery(id+"F0.wireOp",EDGE,"E16.MirrorCS")])],"isStart":true});
            var Q3;
            Q3=makeQuery(id+"F1.opExtrude","CAP_EDGE",EDGE,{"disambiguationData":[OSD([sQuery(id+"F0.wireOp",EDGE,"E17.MirrorCS")])],"isStart":true});
            var Q4;
            {var subQ0=sQuery(id+"F0.wireOp",EDGE,"E26.MirrorCS");var subQ1=sQuery(id+"F0.wireOp",EDGE,"E17.MirrorCS");var subQ2=sQuery(id+"F0.wireOp",EDGE,"E1");Q4=makeQuery(id+"F1.opExtrude","CAP_EDGE",EDGE,{"disambiguationData":[OSD([subQ2]),TDD([makeQuery(id+"F0.imprint","IMPRINT",EDGE,{"disambiguationData":[TD([[makeQuery(id+"F0.imprint","INTERSECT",VERTEX,{"derivedFrom":[subQ2,subQ1]}),-1.0]])],"derivedFrom":subQ2}),makeQuery(id+"F0.imprint","IMPRINT",EDGE,{"disambiguationData":[TD([[makeQuery(id+"F0.imprint","INTERSECT",VERTEX,{"derivedFrom":[subQ2,subQ0]}),1.0]])],"derivedFrom":subQ2})])],"isStart":true});}
            var Q5;
            Q5=makeQuery(id+"F1.opExtrude","CAP_EDGE",EDGE,{"disambiguationData":[OSD([sQuery(id+"F0.wireOp",EDGE,"E26.MirrorCS")])],"isStart":true});
            var Q6;
            Q6=makeQuery(id+"F1.opExtrude","CAP_EDGE",EDGE,{"disambiguationData":[OSD([sQuery(id+"F0.wireOp",EDGE,"E30.MirrorCS")])],"isStart":true});
            var Q7;
            {var subQ0=sQuery(id+"F0.wireOp",EDGE,"E43.MirrorCS");var subQ1=sQuery(id+"F0.wireOp",EDGE,"E30.MirrorCS");var subQ2=sQuery(id+"F0.wireOp",EDGE,"E1");Q7=makeQuery(id+"F1.opExtrude","CAP_EDGE",EDGE,{"disambiguationData":[OSD([subQ2]),TDD([makeQuery(id+"F0.imprint","IMPRINT",EDGE,{"disambiguationData":[TD([[makeQuery(id+"F0.imprint","INTERSECT",VERTEX,{"derivedFrom":[subQ2,subQ1]}),-1.0]])],"derivedFrom":subQ2}),makeQuery(id+"F0.imprint","IMPRINT",EDGE,{"disambiguationData":[TD([[makeQuery(id+"F0.imprint","INTERSECT",VERTEX,{"derivedFrom":[subQ2,subQ0]}),1.0]])],"derivedFrom":subQ2})])],"isStart":true});}
            var Q8;
            Q8=makeQuery(id+"F1.opExtrude","CAP_EDGE",EDGE,{"disambiguationData":[OSD([sQuery(id+"F0.wireOp",EDGE,"E43.MirrorCS")])],"isStart":true});
            var Q9;
            Q9=makeQuery(id+"F1.opExtrude","CAP_EDGE",EDGE,{"disambiguationData":[OSD([sQuery(id+"F0.wireOp",EDGE,"E42")])],"isStart":true});
            var Q10;
            {var subQ0=sQuery(id+"F0.wireOp",EDGE,"E42");var subQ1=sQuery(id+"F0.wireOp",EDGE,"E20.MirrorCS");var subQ2=sQuery(id+"F0.wireOp",EDGE,"E1");Q10=makeQuery(id+"F1.opExtrude","CAP_EDGE",EDGE,{"disambiguationData":[OSD([subQ2]),TDD([makeQuery(id+"F0.imprint","IMPRINT",EDGE,{"disambiguationData":[TD([[makeQuery(id+"F0.imprint","INTERSECT",VERTEX,{"derivedFrom":[subQ2,subQ0]}),-1.0]])],"derivedFrom":subQ2}),makeQuery(id+"F0.imprint","IMPRINT",EDGE,{"disambiguationData":[TD([[makeQuery(id+"F0.imprint","INTERSECT",VERTEX,{"derivedFrom":[subQ2,subQ1]}),1.0]])],"derivedFrom":subQ2})])],"isStart":true});}
            var Q11;
            Q11=makeQuery(id+"F1.opExtrude","CAP_EDGE",EDGE,{"disambiguationData":[OSD([sQuery(id+"F0.wireOp",EDGE,"E20.MirrorCS")])],"isStart":true});
            var Q12;
            Q12=makeQuery(id+"F1.opExtrude","CAP_EDGE",EDGE,{"disambiguationData":[OSD([sQuery(id+"F0.wireOp",EDGE,"E23.MirrorCS")])],"isStart":true});
            var Q13;
            {var subQ0=sQuery(id+"F0.wireOp",EDGE,"E23.MirrorCS");var subQ1=sQuery(id+"F0.wireOp",EDGE,"E13.MirrorCS");var subQ2=sQuery(id+"F0.wireOp",EDGE,"E1");Q13=makeQuery(id+"F1.opExtrude","CAP_EDGE",EDGE,{"disambiguationData":[OSD([subQ2]),TDD([makeQuery(id+"F0.imprint","IMPRINT",EDGE,{"disambiguationData":[TD([[makeQuery(id+"F0.imprint","INTERSECT",VERTEX,{"derivedFrom":[subQ2,subQ1]}),1.0]])],"derivedFrom":subQ2}),makeQuery(id+"F0.imprint","IMPRINT",EDGE,{"disambiguationData":[TD([[makeQuery(id+"F0.imprint","INTERSECT",VERTEX,{"derivedFrom":[subQ2,subQ0]}),-1.0]])],"derivedFrom":subQ2})])],"isStart":true});}
            var Q14;
            Q14=makeQuery(id+"F1.opExtrude","CAP_EDGE",EDGE,{"disambiguationData":[OSD([sQuery(id+"F0.wireOp",EDGE,"E13.MirrorCS")])],"isStart":true});
            var Q15;
            Q15=makeQuery(id+"F1.opExtrude","CAP_EDGE",EDGE,{"disambiguationData":[OSD([sQuery(id+"F0.wireOp",EDGE,"E12")])],"isStart":true});
            var Q16;
            {var subQ0=sQuery(id+"F0.wireOp",EDGE,"E44.MirrorCS");var subQ1=sQuery(id+"F0.wireOp",EDGE,"E12");var subQ2=sQuery(id+"F0.wireOp",EDGE,"E1");Q16=makeQuery(id+"F1.opExtrude","CAP_EDGE",EDGE,{"disambiguationData":[OSD([subQ2]),TDD([makeQuery(id+"F0.imprint","IMPRINT",EDGE,{"disambiguationData":[TD([[makeQuery(id+"F0.imprint","INTERSECT",VERTEX,{"derivedFrom":[subQ2,subQ1]}),-1.0]])],"derivedFrom":subQ2}),makeQuery(id+"F0.imprint","IMPRINT",EDGE,{"disambiguationData":[TD([[makeQuery(id+"F0.imprint","INTERSECT",VERTEX,{"derivedFrom":[subQ2,subQ0]}),1.0]])],"derivedFrom":subQ2})])],"isStart":true});}
            var Q17;
            Q17=makeQuery(id+"F1.opExtrude","CAP_EDGE",EDGE,{"disambiguationData":[OSD([sQuery(id+"F0.wireOp",EDGE,"E44.MirrorCS")])],"isStart":true});
            fillet(context, id + "F7", {"entities" : qUnion([Q0, Q1, Q2, Q3, Q4, Q5, Q6, Q7, Q8, Q9, Q10, Q11, Q12, Q13, Q14, Q15, Q16, Q17]), "radius" : .5 * mm, "tangentPropagation" : true, "allowEdgeOverflow" : false});
        }
    });
